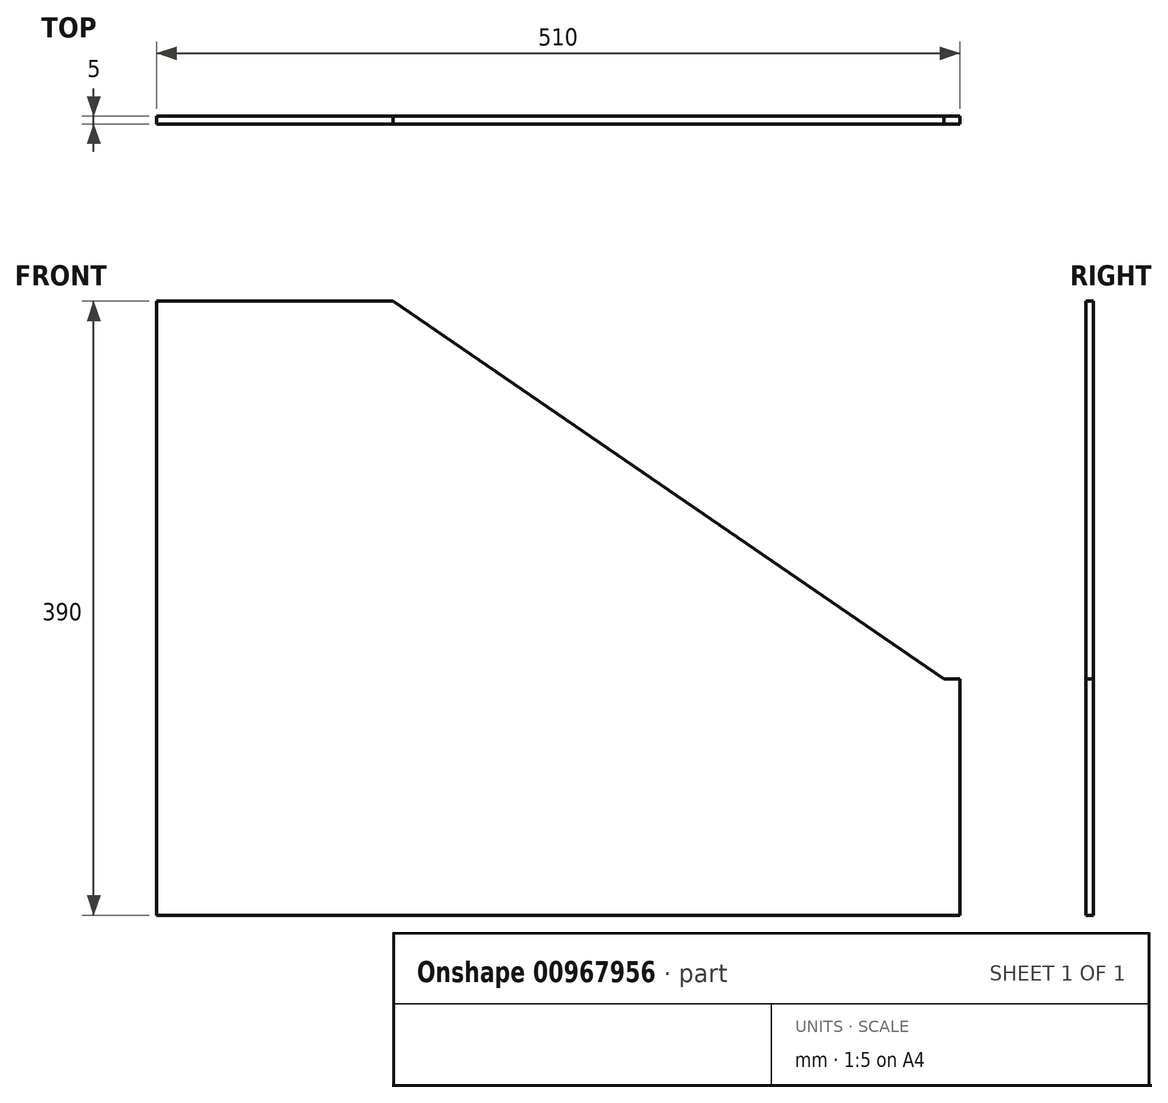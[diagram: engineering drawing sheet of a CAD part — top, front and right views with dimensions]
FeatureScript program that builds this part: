
annotation { "Feature Type Name" : "Feature", "Feature Type Description" : "" }
export const myFeature = defineFeature(function(context is Context, id is Id, definition is map)
    precondition{}
    {
        {
            var Q0;
            Q0=qCreatedBy(makeId("Front.planeOp"),FACE);
            var sketch = newSketch(context, id + "F0", { "sketchPlane" : qUnion([Q0])});
            skLineSegment(sketch, "E0.bottom", {"start": v(250, -195) * mm, "end": v(-250, -195) * mm});
            skLineSegment(sketch, "E0.top", {"start": v(-100, 195) * mm, "end": v(-250, 195) * mm});
            skLineSegment(sketch, "E0.right", {"start": v(-250, -195) * mm, "end": v(-250, 195) * mm});
            skPoint(sketch, "E0.middle", {"position": v(0, 0) * mm});
            skLineSegment(sketch, "E1", {"start": v(-100, 195) * mm, "end": v(250, -45) * mm});
            skLineSegment(sketch, "E2", {"start": v(250, -45) * mm, "end": v(260, -45) * mm});
            skLineSegment(sketch, "E3", {"start": v(260, -45) * mm, "end": v(260, -195) * mm});
            skPoint(sketch, "E4.orphan", {"position": v(250, 195) * mm});
            skLineSegment(sketch, "E5", {"start": v(250, -195) * mm, "end": v(260, -195) * mm});
            skSolve(sketch);
        }
        {
            var Q0;
            Q0 = qSketchRegion(id + "F0", true);
            extrude(context, id + "F1", {"entities" : qUnion([Q0]), "depth" : 5 * mm, "offsetDistance" : 25 * mm});
        }
    });
